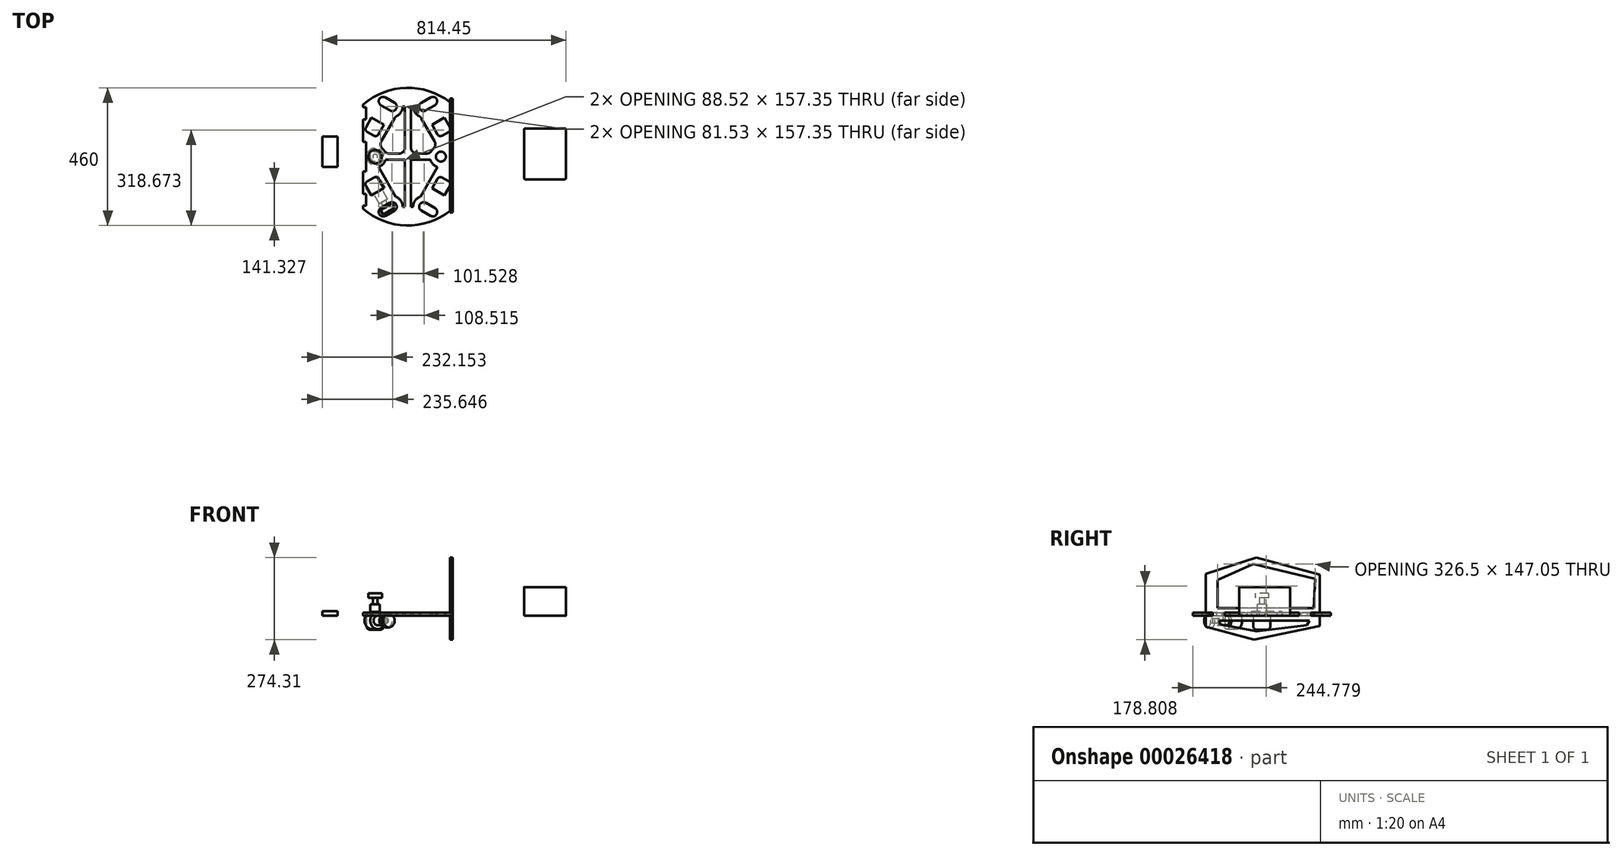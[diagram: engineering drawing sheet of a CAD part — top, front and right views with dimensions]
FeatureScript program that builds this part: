
annotation { "Feature Type Name" : "Feature", "Feature Type Description" : "" }
export const myFeature = defineFeature(function(context is Context, id is Id, definition is map)
    precondition{}
    {
        {
            var Q0;
            Q0=qCreatedBy(makeId("Top.planeOp"),FACE);
            var sketch = newSketch(context, id + "F0", { "sketchPlane" : qUnion([Q0])});
            skCircle(sketch, "E0", {"center": v(0, 0) * mm, "radius": 240 * mm});
            skSolve(sketch);
        }
        {
            var Q0;
            Q0=sQuery(id+"F0.wireOp",EDGE,"E0");
            extrude(context, id + "F1", {"bodyType" : ToolBodyType.SURFACE, "surfaceEntities" : qUnion([Q0]), "depth" : 100 * mm});
        }
        {
            var Q0;
            Q0=qCreatedBy(makeId("Top.planeOp"),FACE);
            var sketch = newSketch(context, id + "F2", { "sketchPlane" : qUnion([Q0])});
            skArc(sketch, "E1", {"start": v(-150, -174.36) * mm, "mid": v(0, -230) * mm, "end": v(150, -174.36) * mm});
            skLineSegment(sketch, "E2", {"start": v(0, -230) * mm, "end": v(0, 230) * mm, "construction": true});
            skLineSegment(sketch, "E3", {"start": v(-150, 174.36) * mm, "end": v(-150, -174.36) * mm});
            skLineSegment(sketch, "E4", {"start": v(150, -174.36) * mm, "end": v(150, 174.36) * mm});
            skArc(sketch, "E5.trimOffspring", {"start": v(150, 174.36) * mm, "mid": v(0, 230) * mm, "end": v(-150, 174.36) * mm});
            skLineSegment(sketch, "E6", {"start": v(0, 0) * mm, "end": v(-150, 0) * mm, "construction": true});
            skCircle(sketch, "E7", {"center": v(-110, 0) * mm, "radius": 16.5 * mm});
            skArc(sketch, "E8.0", {"start": v(-98.52, -34.65) * mm, "mid": v(-83.65, -25.25) * mm, "end": v(-74.9, -10) * mm});
            skArc(sketch, "E9.MirrorC", {"start": v(-98.52, 34.65) * mm, "mid": v(-83.65, 25.25) * mm, "end": v(-74.9, 10) * mm});
            skLineSegment(sketch, "E10.MirrorCS", {"start": v(0, 230) * mm, "end": v(0, -230) * mm, "construction": true});
            skLineSegment(sketch, "E11.MirrorCS", {"start": v(0, 0) * mm, "end": v(150, 0) * mm, "construction": true});
            skArc(sketch, "E12.MirrorC", {"start": v(74.9, -10) * mm, "mid": v(83.65, -25.25) * mm, "end": v(98.52, -34.65) * mm});
            skCircle(sketch, "E13.MirrorC", {"center": v(110, 0) * mm, "radius": 16.5 * mm});
            skLineSegment(sketch, "E14", {"start": v(-45, 180.34) * mm, "end": v(-75.31, 197.84) * mm});
            skLineSegment(sketch, "E15", {"start": v(-60, 154.36) * mm, "end": v(-90.31, 171.86) * mm});
            skArc(sketch, "E16", {"start": v(-75.31, 197.84) * mm, "mid": v(-95.8, 192.35) * mm, "end": v(-90.31, 171.86) * mm});
            skArc(sketch, "E17", {"start": v(-60, 154.36) * mm, "mid": v(-39.5, 159.85) * mm, "end": v(-45, 180.34) * mm});
            skLineSegment(sketch, "E18", {"start": v(-45, 180.34) * mm, "end": v(-60, 154.36) * mm, "construction": true});
            skLineSegment(sketch, "E19", {"start": v(-75.31, 197.84) * mm, "end": v(-90.31, 171.86) * mm, "construction": true});
            skLineSegment(sketch, "E20.MirrorCS", {"start": v(45, 180.34) * mm, "end": v(75.31, 197.84) * mm});
            skLineSegment(sketch, "E21.MirrorCS", {"start": v(45, 180.34) * mm, "end": v(60, 154.36) * mm});
            skArc(sketch, "E22.MirrorCS", {"start": v(75.31, 197.84) * mm, "mid": v(95.8, 192.35) * mm, "end": v(90.31, 171.86) * mm});
            skArc(sketch, "E23.MirrorCS", {"start": v(60, 154.36) * mm, "mid": v(39.5, 159.85) * mm, "end": v(45, 180.34) * mm});
            skLineSegment(sketch, "E24.MirrorCS", {"start": v(75.31, 197.84) * mm, "end": v(90.31, 171.86) * mm});
            skLineSegment(sketch, "E25.MirrorCS", {"start": v(60, 154.36) * mm, "end": v(90.31, 171.86) * mm});
            skLineSegment(sketch, "E26.MirrorCS", {"start": v(-75.31, -197.84) * mm, "end": v(-90.31, -171.86) * mm});
            skLineSegment(sketch, "E27.MirrorCS", {"start": v(-60, -154.36) * mm, "end": v(-90.31, -171.86) * mm});
            skArc(sketch, "E28.MirrorCS", {"start": v(-75.31, -197.84) * mm, "mid": v(-95.8, -192.35) * mm, "end": v(-90.31, -171.86) * mm});
            skLineSegment(sketch, "E29.MirrorCS", {"start": v(-45, -180.34) * mm, "end": v(-60, -154.36) * mm});
            skLineSegment(sketch, "E30.MirrorCS", {"start": v(-45, -180.34) * mm, "end": v(-75.31, -197.84) * mm});
            skArc(sketch, "E31.MirrorCS", {"start": v(-60, -154.36) * mm, "mid": v(-39.5, -159.85) * mm, "end": v(-45, -180.34) * mm});
            skArc(sketch, "E32.MirrorCS", {"start": v(75.31, -197.84) * mm, "mid": v(95.8, -192.35) * mm, "end": v(90.31, -171.86) * mm});
            skLineSegment(sketch, "E33.MirrorCS", {"start": v(45, -180.34) * mm, "end": v(60, -154.36) * mm});
            skLineSegment(sketch, "E34.MirrorCS", {"start": v(60, -154.36) * mm, "end": v(90.31, -171.86) * mm});
            skLineSegment(sketch, "E35.MirrorCS", {"start": v(45, -180.34) * mm, "end": v(75.31, -197.84) * mm});
            skLineSegment(sketch, "E36.MirrorCS", {"start": v(75.31, -197.84) * mm, "end": v(90.31, -171.86) * mm});
            skArc(sketch, "E37.MirrorCS", {"start": v(60, -154.36) * mm, "mid": v(39.5, -159.85) * mm, "end": v(45, -180.34) * mm});
            skLineSegment(sketch, "E38", {"start": v(-60.16, 189.09) * mm, "end": v(-125.16, 76.5) * mm, "construction": true});
            skLineSegment(sketch, "E39", {"start": v(-101.16, 118.07) * mm, "end": v(-80.37, 106.07) * mm});
            skLineSegment(sketch, "E40", {"start": v(-80.37, 106.07) * mm, "end": v(-98.87, 74.03) * mm});
            skLineSegment(sketch, "E41", {"start": v(-113.9, 70) * mm, "end": v(-136.41, 83) * mm});
            skLineSegment(sketch, "E42", {"start": v(-140.44, 98.03) * mm, "end": v(-121.94, 130.07) * mm});
            skLineSegment(sketch, "E43", {"start": v(-101.16, 118.07) * mm, "end": v(-121.94, 130.07) * mm});
            skPoint(sketch, "E44.visualSharp", {"position": v(-145.94, 88.5) * mm});
            skArc(sketch, "E44.filletArc", {"start": v(-140.44, 98.03) * mm, "mid": v(-141.54, 89.68) * mm, "end": v(-136.41, 83) * mm});
            skPoint(sketch, "E45.visualSharp", {"position": v(-104.37, 64.5) * mm});
            skArc(sketch, "E45.filletArc", {"start": v(-113.9, 70) * mm, "mid": v(-105.55, 68.9) * mm, "end": v(-98.87, 74.03) * mm});
            skLineSegment(sketch, "E46.0", {"start": v(-40.98, 134.3) * mm, "end": v(-98.52, 34.65) * mm});
            skArc(sketch, "E47.0", {"start": v(-40.98, 134.3) * mm, "mid": v(-23.97, 147.07) * mm, "end": v(-17.5, 167.35) * mm});
            skArc(sketch, "E48.MirrorCS", {"start": v(40.98, 134.3) * mm, "mid": v(23.97, 147.07) * mm, "end": v(17.5, 167.35) * mm});
            skLineSegment(sketch, "E49.MirrorCS", {"start": v(40.98, 134.3) * mm, "end": v(98.52, 34.65) * mm});
            skLineSegment(sketch, "E50.MirrorCS", {"start": v(80.37, 106.07) * mm, "end": v(98.87, 74.03) * mm});
            skLineSegment(sketch, "E51.MirrorCS", {"start": v(101.16, 118.07) * mm, "end": v(80.37, 106.07) * mm});
            skLineSegment(sketch, "E52.MirrorCS", {"start": v(101.16, 118.07) * mm, "end": v(121.94, 130.07) * mm});
            skLineSegment(sketch, "E53.MirrorCS", {"start": v(113.9, 70) * mm, "end": v(136.41, 83) * mm});
            skArc(sketch, "E54.MirrorCS", {"start": v(140.44, 98.03) * mm, "mid": v(141.54, 89.68) * mm, "end": v(136.41, 83) * mm});
            skLineSegment(sketch, "E55.MirrorCS", {"start": v(140.44, 98.03) * mm, "end": v(121.94, 130.07) * mm});
            skArc(sketch, "E56.MirrorCS", {"start": v(113.9, 70) * mm, "mid": v(105.55, 68.9) * mm, "end": v(98.87, 74.03) * mm});
            skLineSegment(sketch, "E57", {"start": v(-17.5, 167.35) * mm, "end": v(-10, 167.35) * mm});
            skLineSegment(sketch, "E58.MirrorCS", {"start": v(40.98, -134.3) * mm, "end": v(98.52, -34.65) * mm});
            skArc(sketch, "E59.MirrorCS", {"start": v(40.98, -134.3) * mm, "mid": v(23.97, -147.07) * mm, "end": v(17.5, -167.35) * mm});
            skLineSegment(sketch, "E60.MirrorCS", {"start": v(-17.5, -167.35) * mm, "end": v(-10, -167.35) * mm});
            skArc(sketch, "E61.MirrorCS", {"start": v(-40.98, -134.3) * mm, "mid": v(-23.97, -147.07) * mm, "end": v(-17.5, -167.35) * mm});
            skLineSegment(sketch, "E62.MirrorCS", {"start": v(-40.98, -134.3) * mm, "end": v(-98.52, -34.65) * mm});
            skLineSegment(sketch, "E63.MirrorCS", {"start": v(-101.16, -118.07) * mm, "end": v(-80.37, -106.07) * mm});
            skLineSegment(sketch, "E64.MirrorCS", {"start": v(-101.16, -118.07) * mm, "end": v(-121.94, -130.07) * mm});
            skLineSegment(sketch, "E65.MirrorCS", {"start": v(-140.44, -98.03) * mm, "end": v(-121.94, -130.07) * mm});
            skLineSegment(sketch, "E66.MirrorCS", {"start": v(80.37, -106.07) * mm, "end": v(98.87, -74.03) * mm});
            skLineSegment(sketch, "E67.MirrorCS", {"start": v(101.16, -118.07) * mm, "end": v(80.37, -106.07) * mm});
            skLineSegment(sketch, "E68.MirrorCS", {"start": v(101.16, -118.07) * mm, "end": v(121.94, -130.07) * mm});
            skLineSegment(sketch, "E69.MirrorCS", {"start": v(140.44, -98.03) * mm, "end": v(121.94, -130.07) * mm});
            skLineSegment(sketch, "E70.MirrorCS", {"start": v(113.9, -70) * mm, "end": v(136.41, -83) * mm});
            skArc(sketch, "E71.MirrorCS", {"start": v(140.44, -98.03) * mm, "mid": v(141.54, -89.68) * mm, "end": v(136.41, -83) * mm});
            skArc(sketch, "E72.MirrorCS", {"start": v(113.9, -70) * mm, "mid": v(105.55, -68.9) * mm, "end": v(98.87, -74.03) * mm});
            skArc(sketch, "E73.MirrorCS", {"start": v(-113.9, -70) * mm, "mid": v(-105.55, -68.9) * mm, "end": v(-98.87, -74.03) * mm});
            skArc(sketch, "E74.MirrorCS", {"start": v(-140.44, -98.03) * mm, "mid": v(-141.54, -89.68) * mm, "end": v(-136.41, -83) * mm});
            skLineSegment(sketch, "E75.MirrorCS", {"start": v(-113.9, -70) * mm, "end": v(-136.41, -83) * mm});
            skLineSegment(sketch, "E76.MirrorCS", {"start": v(-80.37, -106.07) * mm, "end": v(-98.87, -74.03) * mm});
            skLineSegment(sketch, "E77", {"start": v(-74.9, 10) * mm, "end": v(-10, 10) * mm});
            skLineSegment(sketch, "E78", {"start": v(-74.9, -10) * mm, "end": v(-10, -10) * mm});
            skLineSegment(sketch, "E79", {"start": v(-10, 167.35) * mm, "end": v(-10, 10) * mm});
            skLineSegment(sketch, "E80", {"start": v(10, 167.35) * mm, "end": v(10, 10) * mm});
            skLineSegment(sketch, "E81.trimOffspring", {"start": v(10, 10) * mm, "end": v(74.9, 10) * mm});
            skLineSegment(sketch, "E82.trimOffspring", {"start": v(10, -10) * mm, "end": v(74.9, -10) * mm});
            skLineSegment(sketch, "E83.trimOffspring", {"start": v(10, -10) * mm, "end": v(10, -167.35) * mm});
            skLineSegment(sketch, "E84.trimOffspring", {"start": v(-10, -10) * mm, "end": v(-10, -167.35) * mm});
            skArc(sketch, "E85.trimOffspring", {"start": v(-74.9, -10) * mm, "mid": v(-83.65, -25.25) * mm, "end": v(-98.52, -34.65) * mm});
            skArc(sketch, "E86.trimOffspring", {"start": v(-74.9, 10) * mm, "mid": v(-83.65, 25.25) * mm, "end": v(-98.52, 34.65) * mm});
            skArc(sketch, "E87.trimOffspring", {"start": v(98.52, 34.65) * mm, "mid": v(83.65, 25.25) * mm, "end": v(74.9, 10) * mm});
            skLineSegment(sketch, "E88.trimOffspring", {"start": v(10, 167.35) * mm, "end": v(17.5, 167.35) * mm});
            skLineSegment(sketch, "E89.trimOffspring", {"start": v(10, -167.35) * mm, "end": v(17.5, -167.35) * mm});
            skLineSegment(sketch, "E90", {"start": v(150, 164.36) * mm, "end": v(140.5, 164.36) * mm});
            skLineSegment(sketch, "E91", {"start": v(140.5, 164.36) * mm, "end": v(140.5, 124.36) * mm});
            skLineSegment(sketch, "E92", {"start": v(140.5, 124.36) * mm, "end": v(150, 124.36) * mm});
            skLineSegment(sketch, "E93", {"start": v(150, 50) * mm, "end": v(140.5, 50) * mm});
            skLineSegment(sketch, "E94", {"start": v(140.5, 50) * mm, "end": v(140.5, -50) * mm});
            skLineSegment(sketch, "E95", {"start": v(140.5, -50) * mm, "end": v(150, -50) * mm});
            skLineSegment(sketch, "E96.MirrorCS", {"start": v(150, -164.36) * mm, "end": v(140.5, -164.36) * mm});
            skLineSegment(sketch, "E97.MirrorCS", {"start": v(140.5, -164.36) * mm, "end": v(140.5, -124.36) * mm});
            skLineSegment(sketch, "E98.MirrorCS", {"start": v(140.5, -124.36) * mm, "end": v(150, -124.36) * mm});
            skLineSegment(sketch, "E99.MirrorCS", {"start": v(-140.5, 164.36) * mm, "end": v(-140.5, 124.36) * mm});
            skLineSegment(sketch, "E100.MirrorCS", {"start": v(-140.5, 124.36) * mm, "end": v(-150, 124.36) * mm});
            skLineSegment(sketch, "E101.MirrorCS", {"start": v(-140.5, -124.36) * mm, "end": v(-150, -124.36) * mm});
            skLineSegment(sketch, "E102.MirrorCS", {"start": v(-140.5, -164.36) * mm, "end": v(-140.5, -124.36) * mm});
            skLineSegment(sketch, "E103.MirrorCS", {"start": v(-150, -164.36) * mm, "end": v(-140.5, -164.36) * mm});
            skLineSegment(sketch, "E104.MirrorCS", {"start": v(-140.5, -50) * mm, "end": v(-150, -50) * mm});
            skLineSegment(sketch, "E105.MirrorCS", {"start": v(-140.5, 50) * mm, "end": v(-140.5, -50) * mm});
            skLineSegment(sketch, "E106.MirrorCS", {"start": v(-150, 50) * mm, "end": v(-140.5, 50) * mm});
            skLineSegment(sketch, "E107.MirrorCS", {"start": v(-150, 164.36) * mm, "end": v(-140.5, 164.36) * mm});
            skSolve(sketch);
        }
        {
            var Q0;
            Q0=qCreatedBy(makeId("Top.planeOp"),FACE);
            var sketch = newSketch(context, id + "F3", { "sketchPlane" : qUnion([Q0])});
            skLineSegment(sketch, "E108", {"start": v(-387.18, 3.29) * mm, "end": v(-387.18, 88.29) * mm});
            skLineSegment(sketch, "E109", {"start": v(-387.18, 3.29) * mm, "end": v(-369.68, 3.29) * mm});
            skLineSegment(sketch, "E110", {"start": v(-358.68, 14.29) * mm, "end": v(-358.68, 50.29) * mm});
            skLineSegment(sketch, "E111", {"start": v(-358.68, 50.29) * mm, "end": v(-371.18, 50.29) * mm});
            skLineSegment(sketch, "E112", {"start": v(-371.18, 50.29) * mm, "end": v(-371.18, 88.29) * mm});
            skLineSegment(sketch, "E113", {"start": v(-371.18, 88.29) * mm, "end": v(-387.18, 88.29) * mm});
            skPoint(sketch, "E114.visualSharp", {"position": v(-358.68, 3.29) * mm});
            skArc(sketch, "E114.filletArc", {"start": v(-369.68, 3.29) * mm, "mid": v(-361.9, 6.51) * mm, "end": v(-358.68, 14.29) * mm});
            skLineSegment(sketch, "E115", {"start": v(-379.18, 88.29) * mm, "end": v(-379.18, 109.29) * mm});
            skLineSegment(sketch, "E116", {"start": v(-379.18, 109.29) * mm, "end": v(-364.68, 109.29) * mm});
            skLineSegment(sketch, "E117", {"start": v(-364.68, 109.29) * mm, "end": v(-364.68, 125.29) * mm});
            skLineSegment(sketch, "E118", {"start": v(-364.68, 125.29) * mm, "end": v(-387.18, 125.29) * mm});
            skLineSegment(sketch, "E119", {"start": v(-387.18, 125.29) * mm, "end": v(-387.18, 88.29) * mm});
            skSolve(sketch);
        }
        {
            var Q0;
            Q0=makeQuery(id+"F3.imprint","IMPRINT",FACE,{"disambiguationData":[TD([[makeQuery(id+"F3.imprint","IMPRINT",EDGE,{"derivedFrom":sQuery(id+"F3.wireOp",EDGE,"E108")}),-1.0]])]});
            var Q1;
            Q1=sQuery(id+"F3.wireOp",EDGE,"E108");
            revolve(context, id + "F4", {"entities" : qUnion([Q0]), "axis" : qUnion([Q1]), "revolveType" : RevolveType.FULL});
        }
        {
            var Q0;
            Q0=makeQuery(id+"F4.opRevolve","SWEPT_EDGE",EDGE,{"disambiguationData":[OSD([sQuery(id+"F3.wireOp",EDGE,"E112"),sQuery(id+"F3.wireOp",EDGE,"E113")])]});
            fillet(context, id + "F5", {"entities" : qUnion([Q0]), "radius" : 5 * mm, "tangentPropagation" : true, "allowEdgeOverflow" : false});
        }
        {
            var Q0;
            Q0=makeQuery(id+"F4.opRevolve","SWEPT_BODY",BODY,{"disambiguationData":[OSD([sQuery(id+"F3.wireOp",EDGE,"E108"),sQuery(id+"F3.wireOp",EDGE,"E109"),sQuery(id+"F3.wireOp",EDGE,"E110"),sQuery(id+"F3.wireOp",EDGE,"E111"),sQuery(id+"F3.wireOp",EDGE,"E112"),sQuery(id+"F3.wireOp",EDGE,"E113"),sQuery(id+"F3.wireOp",EDGE,"E114.filletArc")])]});
            var Q1;
            Q1=sQuery(id+"F2.wireOp",EDGE,"E2");
            transform(context, id + "F6", {"entities" : qUnion([Q0]), "transformType" : TransformType.TRANSLATION_3D, "dx" : 281.64 * mm, "dy" : -167.2 * mm, "dz" : 0 * mm, "makeCopy" : false});
        }
        {
            var Q0;
            Q0=qCreatedBy(makeId("Front.planeOp"),FACE);
            var sketch = newSketch(context, id + "F7", { "sketchPlane" : qUnion([Q0])});
            skLineSegment(sketch, "E120", {"start": v(0, 0) * mm, "end": v(0, -137.82) * mm, "construction": true});
            skLineSegment(sketch, "E121", {"start": v(0, 0) * mm, "end": v(-117.5, 0) * mm, "construction": true});
            skSolve(sketch);
        }
        {
            var Q0;
            Q0=makeQuery(id+"F4.opRevolve","SWEPT_BODY",BODY,{"disambiguationData":[OSD([sQuery(id+"F3.wireOp",EDGE,"E108"),sQuery(id+"F3.wireOp",EDGE,"E109"),sQuery(id+"F3.wireOp",EDGE,"E110"),sQuery(id+"F3.wireOp",EDGE,"E111"),sQuery(id+"F3.wireOp",EDGE,"E112"),sQuery(id+"F3.wireOp",EDGE,"E113"),sQuery(id+"F3.wireOp",EDGE,"E114.filletArc")])]});
            var Q1;
            Q1=sQuery(id+"F7.wireOp",EDGE,"E120");
            transform(context, id + "F8", {"entities" : qUnion([Q0]), "transformType" : TransformType.ROTATION, "transformAxis" : qUnion([Q1]), "angle" : 30 * degree, "makeCopy" : false});
        }
        {
            var Q0;
            Q0=makeQuery(id+"F4.opRevolve","SWEPT_BODY",BODY,{"disambiguationData":[OSD([sQuery(id+"F3.wireOp",EDGE,"E108"),sQuery(id+"F3.wireOp",EDGE,"E109"),sQuery(id+"F3.wireOp",EDGE,"E110"),sQuery(id+"F3.wireOp",EDGE,"E111"),sQuery(id+"F3.wireOp",EDGE,"E112"),sQuery(id+"F3.wireOp",EDGE,"E113"),sQuery(id+"F3.wireOp",EDGE,"E114.filletArc")])]});
            transform(context, id + "F9", {"entities" : qUnion([Q0]), "transformType" : TransformType.TRANSLATION_3D, "dx" : 56.73 * mm, "dy" : 199.27 * mm, "dz" : 0 * mm, "makeCopy" : false});
        }
        {
            var Q0;
            Q0=makeQuery(id+"F4.opRevolve","SWEPT_BODY",BODY,{"disambiguationData":[OSD([sQuery(id+"F3.wireOp",EDGE,"E108"),sQuery(id+"F3.wireOp",EDGE,"E109"),sQuery(id+"F3.wireOp",EDGE,"E110"),sQuery(id+"F3.wireOp",EDGE,"E111"),sQuery(id+"F3.wireOp",EDGE,"E112"),sQuery(id+"F3.wireOp",EDGE,"E113"),sQuery(id+"F3.wireOp",EDGE,"E114.filletArc")])]});
            var Q1;
            Q1=sQuery(id+"F7.wireOp",EDGE,"E120");
            transform(context, id + "F10", {"entities" : qUnion([Q0]), "transformType" : TransformType.ROTATION, "transformAxis" : qUnion([Q1]), "angle" : 180 * degree, "makeCopy" : true});
        }
        {
            var Q0;
            Q0=makeQuery(id+"F4.opRevolve","SWEPT_BODY",BODY,{"disambiguationData":[OSD([sQuery(id+"F3.wireOp",EDGE,"E108"),sQuery(id+"F3.wireOp",EDGE,"E109"),sQuery(id+"F3.wireOp",EDGE,"E110"),sQuery(id+"F3.wireOp",EDGE,"E111"),sQuery(id+"F3.wireOp",EDGE,"E112"),sQuery(id+"F3.wireOp",EDGE,"E113"),sQuery(id+"F3.wireOp",EDGE,"E114.filletArc")])]});
            var Q1;
            Q1=makeQuery(id+"F10.opPattern","COPY",BODY,{"derivedFrom":makeQuery(id+"F4.opRevolve","SWEPT_BODY",BODY,{"disambiguationData":[OSD([sQuery(id+"F3.wireOp",EDGE,"E108"),sQuery(id+"F3.wireOp",EDGE,"E109"),sQuery(id+"F3.wireOp",EDGE,"E110"),sQuery(id+"F3.wireOp",EDGE,"E111"),sQuery(id+"F3.wireOp",EDGE,"E112"),sQuery(id+"F3.wireOp",EDGE,"E113"),sQuery(id+"F3.wireOp",EDGE,"E114.filletArc")])]}),"instanceName":"1"});
            var Q2;
            Q2=qCreatedBy(makeId("Right.planeOp"),FACE);
            mirror(context, id + "F11", {"entities" : qUnion([Q0, Q1]), "mirrorPlane" : qUnion([Q2])});
        }
        {
            var Q0;
            Q0=makeQuery(id+"F4.opRevolve","SWEPT_BODY",BODY,{"disambiguationData":[OSD([sQuery(id+"F3.wireOp",EDGE,"E108"),sQuery(id+"F3.wireOp",EDGE,"E109"),sQuery(id+"F3.wireOp",EDGE,"E110"),sQuery(id+"F3.wireOp",EDGE,"E111"),sQuery(id+"F3.wireOp",EDGE,"E112"),sQuery(id+"F3.wireOp",EDGE,"E113"),sQuery(id+"F3.wireOp",EDGE,"E114.filletArc")])]});
            var Q1;
            Q1=makeQuery(id+"F10.opPattern","COPY",BODY,{"derivedFrom":makeQuery(id+"F4.opRevolve","SWEPT_BODY",BODY,{"disambiguationData":[OSD([sQuery(id+"F3.wireOp",EDGE,"E108"),sQuery(id+"F3.wireOp",EDGE,"E109"),sQuery(id+"F3.wireOp",EDGE,"E110"),sQuery(id+"F3.wireOp",EDGE,"E111"),sQuery(id+"F3.wireOp",EDGE,"E112"),sQuery(id+"F3.wireOp",EDGE,"E113"),sQuery(id+"F3.wireOp",EDGE,"E114.filletArc")])]}),"instanceName":"1"});
            var Q2;
            Q2=makeQuery(id+"F11.opPattern","COPY",BODY,{"derivedFrom":makeQuery(id+"F4.opRevolve","SWEPT_BODY",BODY,{"disambiguationData":[OSD([sQuery(id+"F3.wireOp",EDGE,"E108"),sQuery(id+"F3.wireOp",EDGE,"E109"),sQuery(id+"F3.wireOp",EDGE,"E110"),sQuery(id+"F3.wireOp",EDGE,"E111"),sQuery(id+"F3.wireOp",EDGE,"E112"),sQuery(id+"F3.wireOp",EDGE,"E113"),sQuery(id+"F3.wireOp",EDGE,"E114.filletArc")])]}),"instanceName":"1"});
            var Q3;
            Q3=makeQuery(id+"F11.opPattern","COPY",BODY,{"derivedFrom":makeQuery(id+"F10.opPattern","COPY",BODY,{"derivedFrom":makeQuery(id+"F4.opRevolve","SWEPT_BODY",BODY,{"disambiguationData":[OSD([sQuery(id+"F3.wireOp",EDGE,"E108"),sQuery(id+"F3.wireOp",EDGE,"E109"),sQuery(id+"F3.wireOp",EDGE,"E110"),sQuery(id+"F3.wireOp",EDGE,"E111"),sQuery(id+"F3.wireOp",EDGE,"E112"),sQuery(id+"F3.wireOp",EDGE,"E113"),sQuery(id+"F3.wireOp",EDGE,"E114.filletArc")])]}),"instanceName":"1"}),"instanceName":"1"});
            deleteBodies(context, id + "F12", {"entities" : qUnion([Q0, Q1, Q2, Q3])});
        }
        {
            var Q0;
            {var subQ2=sQuery(id+"F3.wireOp",EDGE,"E108");Q0=makeQuery(id+"F3.imprint","IMPRINT",FACE,{"disambiguationData":[TD([[makeQuery(id+"F3.imprint","IMPRINT",EDGE,{"derivedFrom":subQ2}),-1.0]])]});}
            var Q1;
            {var subQ1=sQuery(id+"F3.wireOp",EDGE,"E115");Q1=makeQuery(id+"F3.imprint","IMPRINT",FACE,{"disambiguationData":[TD([[makeQuery(id+"F3.imprint","IMPRINT",EDGE,{"derivedFrom":subQ1}),1.0]])]});}
            var Q2;
            Q2=sQuery(id+"F3.wireOp",EDGE,"E108");
            revolve(context, id + "F13", {"entities" : qUnion([Q0, Q1]), "axis" : qUnion([Q2]), "revolveType" : RevolveType.FULL});
        }
        {
            var Q0;
            Q0=makeQuery(id+"F13.opRevolve","SWEPT_BODY",BODY,{"disambiguationData":[OSD([sQuery(id+"F3.wireOp",EDGE,"E108"),sQuery(id+"F3.wireOp",EDGE,"E109"),sQuery(id+"F3.wireOp",EDGE,"E110"),sQuery(id+"F3.wireOp",EDGE,"E111"),sQuery(id+"F3.wireOp",EDGE,"E112"),sQuery(id+"F3.wireOp",EDGE,"E113"),sQuery(id+"F3.wireOp",EDGE,"E114.filletArc"),sQuery(id+"F3.wireOp",EDGE,"E115"),sQuery(id+"F3.wireOp",EDGE,"E116"),sQuery(id+"F3.wireOp",EDGE,"E117"),sQuery(id+"F3.wireOp",EDGE,"E118"),sQuery(id+"F3.wireOp",EDGE,"E119")])]});
            transform(context, id + "F14", {"entities" : qUnion([Q0]), "transformType" : TransformType.TRANSLATION_3D, "dx" : 289.3 * mm, "dy" : 54.85 * mm, "dz" : 0 * mm, "makeCopy" : false});
        }
        {
            var Q0;
            Q0=makeQuery(id+"F13.opRevolve","SWEPT_BODY",BODY,{"disambiguationData":[OSD([sQuery(id+"F3.wireOp",EDGE,"E108"),sQuery(id+"F3.wireOp",EDGE,"E109"),sQuery(id+"F3.wireOp",EDGE,"E110"),sQuery(id+"F3.wireOp",EDGE,"E111"),sQuery(id+"F3.wireOp",EDGE,"E112"),sQuery(id+"F3.wireOp",EDGE,"E113"),sQuery(id+"F3.wireOp",EDGE,"E114.filletArc"),sQuery(id+"F3.wireOp",EDGE,"E115"),sQuery(id+"F3.wireOp",EDGE,"E116"),sQuery(id+"F3.wireOp",EDGE,"E117"),sQuery(id+"F3.wireOp",EDGE,"E118"),sQuery(id+"F3.wireOp",EDGE,"E119")])]});
            var Q1;
            Q1=sQuery(id+"F7.wireOp",EDGE,"E120");
            transform(context, id + "F15", {"entities" : qUnion([Q0]), "transformType" : TransformType.ROTATION, "transformAxis" : qUnion([Q1]), "angle" : 30 * degree, "makeCopy" : false});
        }
        {
            var Q0;
            Q0=makeQuery(id+"F13.opRevolve","SWEPT_BODY",BODY,{"disambiguationData":[OSD([sQuery(id+"F3.wireOp",EDGE,"E108"),sQuery(id+"F3.wireOp",EDGE,"E109"),sQuery(id+"F3.wireOp",EDGE,"E110"),sQuery(id+"F3.wireOp",EDGE,"E111"),sQuery(id+"F3.wireOp",EDGE,"E112"),sQuery(id+"F3.wireOp",EDGE,"E113"),sQuery(id+"F3.wireOp",EDGE,"E114.filletArc"),sQuery(id+"F3.wireOp",EDGE,"E115"),sQuery(id+"F3.wireOp",EDGE,"E116"),sQuery(id+"F3.wireOp",EDGE,"E117"),sQuery(id+"F3.wireOp",EDGE,"E118"),sQuery(id+"F3.wireOp",EDGE,"E119")])]});
            transform(context, id + "F16", {"entities" : qUnion([Q0]), "transformType" : TransformType.TRANSLATION_3D, "dx" : -80.73 * mm, "dy" : -28.36 * mm, "dz" : 0 * mm, "makeCopy" : false});
        }
        {
            var Q0;
            Q0=makeQuery(id+"F13.opRevolve","SWEPT_BODY",BODY,{"disambiguationData":[OSD([sQuery(id+"F3.wireOp",EDGE,"E108"),sQuery(id+"F3.wireOp",EDGE,"E109"),sQuery(id+"F3.wireOp",EDGE,"E110"),sQuery(id+"F3.wireOp",EDGE,"E111"),sQuery(id+"F3.wireOp",EDGE,"E112"),sQuery(id+"F3.wireOp",EDGE,"E113"),sQuery(id+"F3.wireOp",EDGE,"E114.filletArc"),sQuery(id+"F3.wireOp",EDGE,"E115"),sQuery(id+"F3.wireOp",EDGE,"E116"),sQuery(id+"F3.wireOp",EDGE,"E117"),sQuery(id+"F3.wireOp",EDGE,"E118"),sQuery(id+"F3.wireOp",EDGE,"E119")])]});
            var Q1;
            Q1=qCreatedBy(makeId("Right.planeOp"),FACE);
            mirror(context, id + "F17", {"entities" : qUnion([Q0]), "mirrorPlane" : qUnion([Q1])});
        }
        {
            var Q0;
            Q0=makeQuery(id+"F13.opRevolve","SWEPT_BODY",BODY,{"disambiguationData":[OSD([sQuery(id+"F3.wireOp",EDGE,"E108"),sQuery(id+"F3.wireOp",EDGE,"E109"),sQuery(id+"F3.wireOp",EDGE,"E110"),sQuery(id+"F3.wireOp",EDGE,"E111"),sQuery(id+"F3.wireOp",EDGE,"E112"),sQuery(id+"F3.wireOp",EDGE,"E113"),sQuery(id+"F3.wireOp",EDGE,"E114.filletArc"),sQuery(id+"F3.wireOp",EDGE,"E115"),sQuery(id+"F3.wireOp",EDGE,"E116"),sQuery(id+"F3.wireOp",EDGE,"E117"),sQuery(id+"F3.wireOp",EDGE,"E118"),sQuery(id+"F3.wireOp",EDGE,"E119")])]});
            var Q1;
            Q1=makeQuery(id+"F17.opPattern","COPY",BODY,{"derivedFrom":makeQuery(id+"F13.opRevolve","SWEPT_BODY",BODY,{"disambiguationData":[OSD([sQuery(id+"F3.wireOp",EDGE,"E108"),sQuery(id+"F3.wireOp",EDGE,"E109"),sQuery(id+"F3.wireOp",EDGE,"E110"),sQuery(id+"F3.wireOp",EDGE,"E111"),sQuery(id+"F3.wireOp",EDGE,"E112"),sQuery(id+"F3.wireOp",EDGE,"E113"),sQuery(id+"F3.wireOp",EDGE,"E114.filletArc"),sQuery(id+"F3.wireOp",EDGE,"E115"),sQuery(id+"F3.wireOp",EDGE,"E116"),sQuery(id+"F3.wireOp",EDGE,"E117"),sQuery(id+"F3.wireOp",EDGE,"E118"),sQuery(id+"F3.wireOp",EDGE,"E119")])]}),"instanceName":"1"});
            var Q2;
            Q2=qCreatedBy(makeId("Front.planeOp"),FACE);
            mirror(context, id + "F18", {"entities" : qUnion([Q0, Q1]), "mirrorPlane" : qUnion([Q2])});
        }
        {
            var Q0;
            Q0=makeQuery(id+"F13.opRevolve","SWEPT_BODY",BODY,{"disambiguationData":[OSD([sQuery(id+"F3.wireOp",EDGE,"E108"),sQuery(id+"F3.wireOp",EDGE,"E109"),sQuery(id+"F3.wireOp",EDGE,"E110"),sQuery(id+"F3.wireOp",EDGE,"E111"),sQuery(id+"F3.wireOp",EDGE,"E112"),sQuery(id+"F3.wireOp",EDGE,"E113"),sQuery(id+"F3.wireOp",EDGE,"E114.filletArc"),sQuery(id+"F3.wireOp",EDGE,"E115"),sQuery(id+"F3.wireOp",EDGE,"E116"),sQuery(id+"F3.wireOp",EDGE,"E117"),sQuery(id+"F3.wireOp",EDGE,"E118"),sQuery(id+"F3.wireOp",EDGE,"E119")])]});
            var Q1;
            Q1=sQuery(id+"F7.wireOp",EDGE,"E120");
            transform(context, id + "F19", {"entities" : qUnion([Q0]), "transformType" : TransformType.ROTATION, "transformAxis" : qUnion([Q1]), "angle" : 30 * degree, "oppositeDirection" : true, "makeCopy" : false});
        }
        {
            var Q0;
            Q0=makeQuery(id+"F13.opRevolve","SWEPT_BODY",BODY,{"disambiguationData":[OSD([sQuery(id+"F3.wireOp",EDGE,"E108"),sQuery(id+"F3.wireOp",EDGE,"E109"),sQuery(id+"F3.wireOp",EDGE,"E110"),sQuery(id+"F3.wireOp",EDGE,"E111"),sQuery(id+"F3.wireOp",EDGE,"E112"),sQuery(id+"F3.wireOp",EDGE,"E113"),sQuery(id+"F3.wireOp",EDGE,"E114.filletArc"),sQuery(id+"F3.wireOp",EDGE,"E115"),sQuery(id+"F3.wireOp",EDGE,"E116"),sQuery(id+"F3.wireOp",EDGE,"E117"),sQuery(id+"F3.wireOp",EDGE,"E118"),sQuery(id+"F3.wireOp",EDGE,"E119")])]});
            var Q1;
            Q1=sQuery(id+"F7.wireOp",EDGE,"E120");
            transform(context, id + "F20", {"entities" : qUnion([Q0]), "transformType" : TransformType.ROTATION, "transformAxis" : qUnion([Q1]), "angle" : 30 * degree, "makeCopy" : true});
        }
        {
            var Q0;
            Q0=makeQuery(id+"F13.opRevolve","SWEPT_BODY",BODY,{"disambiguationData":[OSD([sQuery(id+"F3.wireOp",EDGE,"E108"),sQuery(id+"F3.wireOp",EDGE,"E109"),sQuery(id+"F3.wireOp",EDGE,"E110"),sQuery(id+"F3.wireOp",EDGE,"E111"),sQuery(id+"F3.wireOp",EDGE,"E112"),sQuery(id+"F3.wireOp",EDGE,"E113"),sQuery(id+"F3.wireOp",EDGE,"E114.filletArc"),sQuery(id+"F3.wireOp",EDGE,"E115"),sQuery(id+"F3.wireOp",EDGE,"E116"),sQuery(id+"F3.wireOp",EDGE,"E117"),sQuery(id+"F3.wireOp",EDGE,"E118"),sQuery(id+"F3.wireOp",EDGE,"E119")])]});
            var Q1;
            Q1=sQuery(id+"F7.wireOp",EDGE,"E121");
            transform(context, id + "F21", {"entities" : qUnion([Q0]), "transformType" : TransformType.ROTATION, "transformAxis" : qUnion([Q1]), "angle" : 90 * degree, "makeCopy" : false});
        }
        {
            var Q0;
            Q0=makeQuery(id+"F13.opRevolve","SWEPT_BODY",BODY,{"disambiguationData":[OSD([sQuery(id+"F3.wireOp",EDGE,"E108"),sQuery(id+"F3.wireOp",EDGE,"E109"),sQuery(id+"F3.wireOp",EDGE,"E110"),sQuery(id+"F3.wireOp",EDGE,"E111"),sQuery(id+"F3.wireOp",EDGE,"E112"),sQuery(id+"F3.wireOp",EDGE,"E113"),sQuery(id+"F3.wireOp",EDGE,"E114.filletArc"),sQuery(id+"F3.wireOp",EDGE,"E115"),sQuery(id+"F3.wireOp",EDGE,"E116"),sQuery(id+"F3.wireOp",EDGE,"E117"),sQuery(id+"F3.wireOp",EDGE,"E118"),sQuery(id+"F3.wireOp",EDGE,"E119")])]});
            transform(context, id + "F22", {"entities" : qUnion([Q0]), "transformType" : TransformType.TRANSLATION_3D, "dx" : 45.2 * mm, "dy" : 0 * mm, "dz" : 0 * mm, "makeCopy" : false});
        }
        {
            var Q0;
            Q0=makeQuery(id+"F13.opRevolve","SWEPT_BODY",BODY,{"disambiguationData":[OSD([sQuery(id+"F3.wireOp",EDGE,"E108"),sQuery(id+"F3.wireOp",EDGE,"E109"),sQuery(id+"F3.wireOp",EDGE,"E110"),sQuery(id+"F3.wireOp",EDGE,"E111"),sQuery(id+"F3.wireOp",EDGE,"E112"),sQuery(id+"F3.wireOp",EDGE,"E113"),sQuery(id+"F3.wireOp",EDGE,"E114.filletArc"),sQuery(id+"F3.wireOp",EDGE,"E115"),sQuery(id+"F3.wireOp",EDGE,"E116"),sQuery(id+"F3.wireOp",EDGE,"E117"),sQuery(id+"F3.wireOp",EDGE,"E118"),sQuery(id+"F3.wireOp",EDGE,"E119")])]});
            var Q1;
            Q1=qCreatedBy(makeId("Right.planeOp"),FACE);
            mirror(context, id + "F23", {"entities" : qUnion([Q0]), "mirrorPlane" : qUnion([Q1])});
        }
        {
            var Q0;
            {var subQ10=sQuery(id+"F2.wireOp",EDGE,"E1");Q0=makeQuery(id+"F2.imprint","IMPRINT",FACE,{"disambiguationData":[TD([[makeQuery(id+"F2.imprint","IMPRINT",EDGE,{"derivedFrom":subQ10}),1.0]])]});}
            extrude(context, id + "F24", {"entities" : qUnion([Q0]), "depth" : 9.5 * mm});
        }
        {
            var Q0;
            Q0=makeQuery(id+"F18.opPattern","COPY",BODY,{"derivedFrom":makeQuery(id+"F13.opRevolve","SWEPT_BODY",BODY,{"disambiguationData":[OSD([sQuery(id+"F3.wireOp",EDGE,"E108"),sQuery(id+"F3.wireOp",EDGE,"E109"),sQuery(id+"F3.wireOp",EDGE,"E110"),sQuery(id+"F3.wireOp",EDGE,"E111"),sQuery(id+"F3.wireOp",EDGE,"E112"),sQuery(id+"F3.wireOp",EDGE,"E113"),sQuery(id+"F3.wireOp",EDGE,"E114.filletArc"),sQuery(id+"F3.wireOp",EDGE,"E115"),sQuery(id+"F3.wireOp",EDGE,"E116"),sQuery(id+"F3.wireOp",EDGE,"E117"),sQuery(id+"F3.wireOp",EDGE,"E118"),sQuery(id+"F3.wireOp",EDGE,"E119")])]}),"instanceName":"1"});
            transform(context, id + "F25", {"entities" : qUnion([Q0]), "transformType" : TransformType.TRANSLATION_3D, "dx" : 9.08 * mm, "dy" : -6.75 * mm, "dz" : -10.16 * mm, "makeCopy" : false});
        }
        {
            var Q0;
            Q0=makeQuery(id+"F18.opPattern","COPY",BODY,{"derivedFrom":makeQuery(id+"F13.opRevolve","SWEPT_BODY",BODY,{"disambiguationData":[OSD([sQuery(id+"F3.wireOp",EDGE,"E108"),sQuery(id+"F3.wireOp",EDGE,"E109"),sQuery(id+"F3.wireOp",EDGE,"E110"),sQuery(id+"F3.wireOp",EDGE,"E111"),sQuery(id+"F3.wireOp",EDGE,"E112"),sQuery(id+"F3.wireOp",EDGE,"E113"),sQuery(id+"F3.wireOp",EDGE,"E114.filletArc"),sQuery(id+"F3.wireOp",EDGE,"E115"),sQuery(id+"F3.wireOp",EDGE,"E116"),sQuery(id+"F3.wireOp",EDGE,"E117"),sQuery(id+"F3.wireOp",EDGE,"E118"),sQuery(id+"F3.wireOp",EDGE,"E119")])]}),"instanceName":"1"});
            transform(context, id + "F26", {"entities" : qUnion([Q0]), "transformType" : TransformType.TRANSLATION_3D, "dx" : 0 * mm, "dy" : 0 * mm, "dz" : -6.64 * mm, "makeCopy" : false});
        }
        {
            var Q0;
            Q0=makeQuery(id+"F18.opPattern","COPY",BODY,{"derivedFrom":makeQuery(id+"F13.opRevolve","SWEPT_BODY",BODY,{"disambiguationData":[OSD([sQuery(id+"F3.wireOp",EDGE,"E108"),sQuery(id+"F3.wireOp",EDGE,"E109"),sQuery(id+"F3.wireOp",EDGE,"E110"),sQuery(id+"F3.wireOp",EDGE,"E111"),sQuery(id+"F3.wireOp",EDGE,"E112"),sQuery(id+"F3.wireOp",EDGE,"E113"),sQuery(id+"F3.wireOp",EDGE,"E114.filletArc"),sQuery(id+"F3.wireOp",EDGE,"E115"),sQuery(id+"F3.wireOp",EDGE,"E116"),sQuery(id+"F3.wireOp",EDGE,"E117"),sQuery(id+"F3.wireOp",EDGE,"E118"),sQuery(id+"F3.wireOp",EDGE,"E119")])]}),"instanceName":"1"});
            transform(context, id + "F27", {"entities" : qUnion([Q0]), "transformType" : TransformType.TRANSLATION_3D, "dx" : 2.58 * mm, "dy" : 1.8 * mm, "dz" : 0 * mm, "makeCopy" : false});
        }
        {
            var Q0;
            Q0=makeQuery(id+"F20.opPattern","COPY",BODY,{"derivedFrom":makeQuery(id+"F13.opRevolve","SWEPT_BODY",BODY,{"disambiguationData":[OSD([sQuery(id+"F3.wireOp",EDGE,"E108"),sQuery(id+"F3.wireOp",EDGE,"E109"),sQuery(id+"F3.wireOp",EDGE,"E110"),sQuery(id+"F3.wireOp",EDGE,"E111"),sQuery(id+"F3.wireOp",EDGE,"E112"),sQuery(id+"F3.wireOp",EDGE,"E113"),sQuery(id+"F3.wireOp",EDGE,"E114.filletArc"),sQuery(id+"F3.wireOp",EDGE,"E115"),sQuery(id+"F3.wireOp",EDGE,"E116"),sQuery(id+"F3.wireOp",EDGE,"E117"),sQuery(id+"F3.wireOp",EDGE,"E118"),sQuery(id+"F3.wireOp",EDGE,"E119")])]}),"instanceName":"1"});
            deleteBodies(context, id + "F28", {"entities" : qUnion([Q0])});
        }
        {
            var Q0;
            Q0=makeQuery(id+"F23.opPattern","COPY",BODY,{"derivedFrom":makeQuery(id+"F13.opRevolve","SWEPT_BODY",BODY,{"disambiguationData":[OSD([sQuery(id+"F3.wireOp",EDGE,"E108"),sQuery(id+"F3.wireOp",EDGE,"E109"),sQuery(id+"F3.wireOp",EDGE,"E110"),sQuery(id+"F3.wireOp",EDGE,"E111"),sQuery(id+"F3.wireOp",EDGE,"E112"),sQuery(id+"F3.wireOp",EDGE,"E113"),sQuery(id+"F3.wireOp",EDGE,"E114.filletArc"),sQuery(id+"F3.wireOp",EDGE,"E115"),sQuery(id+"F3.wireOp",EDGE,"E116"),sQuery(id+"F3.wireOp",EDGE,"E117"),sQuery(id+"F3.wireOp",EDGE,"E118"),sQuery(id+"F3.wireOp",EDGE,"E119")])]}),"instanceName":"1"});
            var Q1;
            Q1=makeQuery(id+"F18.opPattern","COPY",BODY,{"derivedFrom":makeQuery(id+"F17.opPattern","COPY",BODY,{"derivedFrom":makeQuery(id+"F13.opRevolve","SWEPT_BODY",BODY,{"disambiguationData":[OSD([sQuery(id+"F3.wireOp",EDGE,"E108"),sQuery(id+"F3.wireOp",EDGE,"E109"),sQuery(id+"F3.wireOp",EDGE,"E110"),sQuery(id+"F3.wireOp",EDGE,"E111"),sQuery(id+"F3.wireOp",EDGE,"E112"),sQuery(id+"F3.wireOp",EDGE,"E113"),sQuery(id+"F3.wireOp",EDGE,"E114.filletArc"),sQuery(id+"F3.wireOp",EDGE,"E115"),sQuery(id+"F3.wireOp",EDGE,"E116"),sQuery(id+"F3.wireOp",EDGE,"E117"),sQuery(id+"F3.wireOp",EDGE,"E118"),sQuery(id+"F3.wireOp",EDGE,"E119")])]}),"instanceName":"1"}),"instanceName":"1"});
            deleteBodies(context, id + "F29", {"entities" : qUnion([Q0, Q1])});
        }
        {
            var Q0;
            Q0=makeQuery(id+"F17.opPattern","COPY",BODY,{"derivedFrom":makeQuery(id+"F13.opRevolve","SWEPT_BODY",BODY,{"disambiguationData":[OSD([sQuery(id+"F3.wireOp",EDGE,"E108"),sQuery(id+"F3.wireOp",EDGE,"E109"),sQuery(id+"F3.wireOp",EDGE,"E110"),sQuery(id+"F3.wireOp",EDGE,"E111"),sQuery(id+"F3.wireOp",EDGE,"E112"),sQuery(id+"F3.wireOp",EDGE,"E113"),sQuery(id+"F3.wireOp",EDGE,"E114.filletArc"),sQuery(id+"F3.wireOp",EDGE,"E115"),sQuery(id+"F3.wireOp",EDGE,"E116"),sQuery(id+"F3.wireOp",EDGE,"E117"),sQuery(id+"F3.wireOp",EDGE,"E118"),sQuery(id+"F3.wireOp",EDGE,"E119")])]}),"instanceName":"1"});
            deleteBodies(context, id + "F30", {"entities" : qUnion([Q0])});
        }
        {
            var Q0;
            Q0=makeQuery(id+"F13.opRevolve","SWEPT_BODY",BODY,{"disambiguationData":[OSD([sQuery(id+"F3.wireOp",EDGE,"E108"),sQuery(id+"F3.wireOp",EDGE,"E109"),sQuery(id+"F3.wireOp",EDGE,"E110"),sQuery(id+"F3.wireOp",EDGE,"E111"),sQuery(id+"F3.wireOp",EDGE,"E112"),sQuery(id+"F3.wireOp",EDGE,"E113"),sQuery(id+"F3.wireOp",EDGE,"E114.filletArc"),sQuery(id+"F3.wireOp",EDGE,"E115"),sQuery(id+"F3.wireOp",EDGE,"E116"),sQuery(id+"F3.wireOp",EDGE,"E117"),sQuery(id+"F3.wireOp",EDGE,"E118"),sQuery(id+"F3.wireOp",EDGE,"E119")])]});
            var Q1;
            Q1=sQuery(id+"F7.wireOp",EDGE,"E121");
            transform(context, id + "F31", {"entities" : qUnion([Q0]), "transformType" : TransformType.ROTATION, "transformAxis" : qUnion([Q1]), "angle" : 180 * degree, "makeCopy" : false});
        }
        {
            var Q0;
            Q0=makeQuery(id+"F13.opRevolve","SWEPT_BODY",BODY,{"disambiguationData":[OSD([sQuery(id+"F3.wireOp",EDGE,"E108"),sQuery(id+"F3.wireOp",EDGE,"E109"),sQuery(id+"F3.wireOp",EDGE,"E110"),sQuery(id+"F3.wireOp",EDGE,"E111"),sQuery(id+"F3.wireOp",EDGE,"E112"),sQuery(id+"F3.wireOp",EDGE,"E113"),sQuery(id+"F3.wireOp",EDGE,"E114.filletArc"),sQuery(id+"F3.wireOp",EDGE,"E115"),sQuery(id+"F3.wireOp",EDGE,"E116"),sQuery(id+"F3.wireOp",EDGE,"E117"),sQuery(id+"F3.wireOp",EDGE,"E118"),sQuery(id+"F3.wireOp",EDGE,"E119")])]});
            transform(context, id + "F32", {"entities" : qUnion([Q0]), "transformType" : TransformType.TRANSLATION_3D, "dx" : -1.32 * mm, "dy" : 0 * mm, "dz" : -40.36 * mm, "makeCopy" : false});
        }
        {
            var Q0;
            Q0=makeQuery(id+"F24.opExtrude","SWEPT_EDGE",EDGE,{"disambiguationData":[OSD([sQuery(id+"F2.wireOp",EDGE,"E49.MirrorCS"),sQuery(id+"F2.wireOp",EDGE,"E87.trimOffspring")])]});
            var Q1;
            Q1=makeQuery(id+"F24.opExtrude","SWEPT_EDGE",EDGE,{"disambiguationData":[OSD([sQuery(id+"F2.wireOp",EDGE,"E81.trimOffspring"),sQuery(id+"F2.wireOp",EDGE,"E87.trimOffspring")])]});
            var Q2;
            Q2=makeQuery(id+"F24.opExtrude","SWEPT_EDGE",EDGE,{"disambiguationData":[OSD([sQuery(id+"F2.wireOp",EDGE,"E48.MirrorCS"),sQuery(id+"F2.wireOp",EDGE,"E49.MirrorCS")])]});
            var Q3;
            Q3=makeQuery(id+"F24.opExtrude","SWEPT_EDGE",EDGE,{"disambiguationData":[OSD([sQuery(id+"F2.wireOp",EDGE,"E80"),sQuery(id+"F2.wireOp",EDGE,"E81.trimOffspring")])]});
            var Q4;
            Q4=makeQuery(id+"F24.opExtrude","SWEPT_EDGE",EDGE,{"disambiguationData":[OSD([sQuery(id+"F2.wireOp",EDGE,"E77"),sQuery(id+"F2.wireOp",EDGE,"E79")])]});
            var Q5;
            Q5=makeQuery(id+"F24.opExtrude","SWEPT_EDGE",EDGE,{"disambiguationData":[OSD([sQuery(id+"F2.wireOp",EDGE,"E77"),sQuery(id+"F2.wireOp",EDGE,"E86.trimOffspring")])]});
            var Q6;
            Q6=makeQuery(id+"F24.opExtrude","SWEPT_EDGE",EDGE,{"disambiguationData":[OSD([sQuery(id+"F2.wireOp",EDGE,"E46.0"),sQuery(id+"F2.wireOp",EDGE,"E86.trimOffspring")])]});
            var Q7;
            Q7=makeQuery(id+"F24.opExtrude","SWEPT_EDGE",EDGE,{"disambiguationData":[OSD([sQuery(id+"F2.wireOp",EDGE,"E46.0"),sQuery(id+"F2.wireOp",EDGE,"E47.0")])]});
            fillet(context, id + "F33", {"entities" : qUnion([Q0, Q1, Q2, Q3, Q4, Q5, Q6, Q7]), "radius" : 20 * mm, "tangentPropagation" : true, "allowEdgeOverflow" : false});
        }
        {
            var Q0;
            Q0=qCreatedBy(makeId("Top.planeOp"),FACE);
            var sketch = newSketch(context, id + "F34", { "sketchPlane" : qUnion([Q0])});
            skLineSegment(sketch, "E122", {"start": v(524.04, 94.21) * mm, "end": v(392.04, 94.21) * mm});
            skLineSegment(sketch, "E123", {"start": v(388.04, 90.21) * mm, "end": v(388.04, -71.79) * mm});
            skLineSegment(sketch, "E124", {"start": v(392.04, -75.79) * mm, "end": v(524.04, -75.79) * mm});
            skLineSegment(sketch, "E125", {"start": v(528.04, -71.79) * mm, "end": v(528.04, 90.21) * mm});
            skPoint(sketch, "E126.visualSharp", {"position": v(528.04, 94.21) * mm});
            skArc(sketch, "E126.filletArc", {"start": v(528.04, 90.21) * mm, "mid": v(526.87, 93.04) * mm, "end": v(524.04, 94.21) * mm});
            skPoint(sketch, "E127.visualSharp", {"position": v(388.04, 94.21) * mm});
            skArc(sketch, "E127.filletArc", {"start": v(392.04, 94.21) * mm, "mid": v(389.21, 93.04) * mm, "end": v(388.04, 90.21) * mm});
            skPoint(sketch, "E128.visualSharp", {"position": v(388.04, -75.79) * mm});
            skArc(sketch, "E128.filletArc", {"start": v(388.04, -71.79) * mm, "mid": v(389.21, -74.62) * mm, "end": v(392.04, -75.79) * mm});
            skPoint(sketch, "E129.visualSharp", {"position": v(528.04, -75.79) * mm});
            skArc(sketch, "E129.filletArc", {"start": v(524.04, -75.79) * mm, "mid": v(526.87, -74.62) * mm, "end": v(528.04, -71.79) * mm});
            skSolve(sketch);
        }
        {
            var Q0;
            Q0=makeQuery(id+"F34.imprint","IMPRINT",FACE,{"disambiguationData":[TD([[makeQuery(id+"F34.imprint","IMPRINT",EDGE,{"derivedFrom":sQuery(id+"F34.wireOp",EDGE,"E122")}),1.0]])]});
            extrude(context, id + "F35", {"entities" : qUnion([Q0]), "depth" : 95 * mm});
        }
        {
            var Q0;
            {var subQ0=sQuery(id+"F2.wireOp",EDGE,"E4");Q0=makeQuery(id+"F24.opExtrude","SWEPT_FACE",FACE,{"disambiguationData":[OSD([subQ0]),TDD([makeQuery(id+"F2.imprint","IMPRINT",EDGE,{"disambiguationData":[TD([[makeQuery(id+"F2.imprint","INTERSECT",VERTEX,{"derivedFrom":[subQ0,sQuery(id+"F2.wireOp",EDGE,"E95")]}),1.0]])],"derivedFrom":subQ0})])]});}
            var sketch = newSketch(context, id + "F36", { "sketchPlane" : qUnion([Q0])});
            skLineSegment(sketch, "E130.0", {"start": v(-164.36, 9.5) * mm, "end": v(-164.36, 0) * mm});
            skLineSegment(sketch, "E131.0", {"start": v(-124.36, 9.5) * mm, "end": v(-124.36, 0) * mm});
            skLineSegment(sketch, "E132.0", {"start": v(-50, 9.5) * mm, "end": v(-50, 0) * mm});
            skLineSegment(sketch, "E133.0", {"start": v(50, 9.5) * mm, "end": v(50, 0) * mm});
            skLineSegment(sketch, "E134.0", {"start": v(124.36, 9.5) * mm, "end": v(124.36, 0) * mm});
            skLineSegment(sketch, "E135.0", {"start": v(164.36, 9.5) * mm, "end": v(164.36, 0) * mm});
            skLineSegment(sketch, "E136", {"start": v(-186.8, 0) * mm, "end": v(-186.8, 138.73) * mm});
            skLineSegment(sketch, "E137", {"start": v(-186.8, 138.73) * mm, "end": v(-18.93, 193.84) * mm});
            skLineSegment(sketch, "E138", {"start": v(-18.93, 193.84) * mm, "end": v(194.23, 136.91) * mm});
            skLineSegment(sketch, "E139", {"start": v(194.23, 136.91) * mm, "end": v(194.23, 0) * mm});
            skLineSegment(sketch, "E140", {"start": v(-186.8, 0) * mm, "end": v(-186.8, -37.84) * mm});
            skLineSegment(sketch, "E141", {"start": v(-186.8, -37.84) * mm, "end": v(-26.57, -80.47) * mm});
            skLineSegment(sketch, "E142", {"start": v(-26.57, -80.47) * mm, "end": v(194.23, -34.86) * mm});
            skLineSegment(sketch, "E143", {"start": v(194.23, -34.86) * mm, "end": v(194.23, 0) * mm});
            skLineSegment(sketch, "E144", {"start": v(-148.47, 119.44) * mm, "end": v(-28.27, 171.86) * mm});
            skLineSegment(sketch, "E145", {"start": v(-28.27, 171.86) * mm, "end": v(178.03, 123.27) * mm});
            skLineSegment(sketch, "E146", {"start": v(178.03, 123.27) * mm, "end": v(173.34, 24.81) * mm});
            skLineSegment(sketch, "E147", {"start": v(173.34, 24.81) * mm, "end": v(-148.47, 24.81) * mm});
            skLineSegment(sketch, "E148", {"start": v(-148.47, 24.81) * mm, "end": v(-148.47, 119.44) * mm});
            skLineSegment(sketch, "E149", {"start": v(-141.22, -16.96) * mm, "end": v(158.85, -16.96) * mm});
            skLineSegment(sketch, "E150", {"start": v(158.85, -16.96) * mm, "end": v(149.9, -32.73) * mm});
            skLineSegment(sketch, "E151", {"start": v(149.9, -32.73) * mm, "end": v(-17.19, -52.34) * mm});
            skLineSegment(sketch, "E152", {"start": v(-17.19, -52.34) * mm, "end": v(-138.67, -29.75) * mm});
            skLineSegment(sketch, "E153", {"start": v(-138.67, -29.75) * mm, "end": v(-141.22, -16.96) * mm});
            skLineSegment(sketch, "E154", {"start": v(-124.36, 9.5) * mm, "end": v(-50, 9.5) * mm});
            skLineSegment(sketch, "E155", {"start": v(50, 9.5) * mm, "end": v(124.36, 9.5) * mm});
            skLineSegment(sketch, "E156", {"start": v(-124.36, 0) * mm, "end": v(-50, 0) * mm});
            skLineSegment(sketch, "E157", {"start": v(50, 0) * mm, "end": v(124.36, 0) * mm});
            skLineSegment(sketch, "E158", {"start": v(-164.36, 0) * mm, "end": v(-186.8, 0) * mm});
            skLineSegment(sketch, "E159", {"start": v(-164.36, 9.5) * mm, "end": v(-186.8, 9.5) * mm});
            skLineSegment(sketch, "E160", {"start": v(164.36, 9.5) * mm, "end": v(194.23, 9.5) * mm});
            skLineSegment(sketch, "E161", {"start": v(164.36, 0) * mm, "end": v(194.23, 0) * mm});
            skSolve(sketch);
        }
        {
            var Q0;
            Q0=qCreatedBy(makeId("Top.planeOp"),FACE);
            var sketch = newSketch(context, id + "F37", { "sketchPlane" : qUnion([Q0])});
            skLineSegment(sketch, "E162", {"start": v(-285.98, 66.63) * mm, "end": v(-235.61, 66.63) * mm});
            skLineSegment(sketch, "E163", {"start": v(-235.61, 66.63) * mm, "end": v(-235.61, -34.97) * mm});
            skLineSegment(sketch, "E164", {"start": v(-235.61, -34.97) * mm, "end": v(-286.41, -34.97) * mm});
            skLineSegment(sketch, "E165", {"start": v(-286.41, -34.97) * mm, "end": v(-285.98, 66.63) * mm});
            skSolve(sketch);
        }
        {
            var Q0;
            Q0=makeQuery(id+"F37.imprint","IMPRINT",FACE,{"disambiguationData":[TD([[makeQuery(id+"F37.imprint","IMPRINT",EDGE,{"derivedFrom":sQuery(id+"F37.wireOp",EDGE,"E162")}),-1.0]])]});
            extrude(context, id + "F38", {"entities" : qUnion([Q0]), "depth" : 15 * mm});
        }
        {
            var Q0;
            Q0=makeQuery(id+"F36.imprint","IMPRINT",FACE,{"disambiguationData":[TD([[makeQuery(id+"F36.imprint","IMPRINT",EDGE,{"derivedFrom":sQuery(id+"F36.wireOp",EDGE,"E130.0")}),1.0]])]});
            extrude(context, id + "F39", {"entities" : qUnion([Q0]), "oppositeDirection" : true, "depth" : 9.1 * mm});
        }
    });
